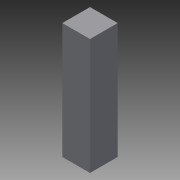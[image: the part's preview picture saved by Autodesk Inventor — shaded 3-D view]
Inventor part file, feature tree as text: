
AUTODESK INVENTOR PART (.ipt)
format: ipt  version: 2013 (Build 170138000, 138)  size: 64,512 bytes
history: native  units: mm
features: extrude x1, sketch x1
ambient origin geometry x8: Origin, YZ Plane, XZ Plane, XY Plane, X Axis, Y Axis, Z Axis, Center Point
bodies: Volumenkörper1 (feature_tree)
feature tree (2):
  extrude  "Extrusion1"  Depth=16.0mm
  sketch  "Skizze1"  dims[d0=16.0mm d2=16.0mm d3=67.0mm d4=0.0mm]
